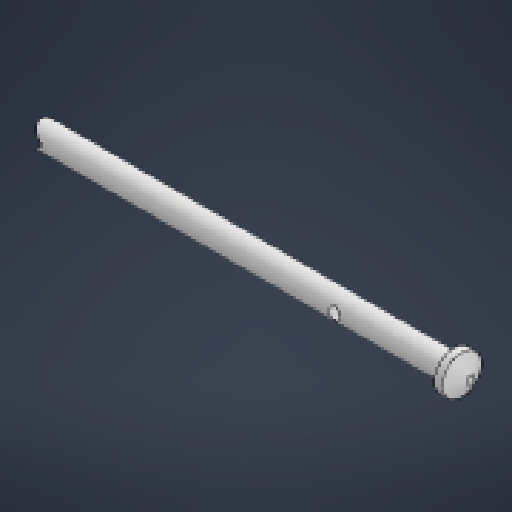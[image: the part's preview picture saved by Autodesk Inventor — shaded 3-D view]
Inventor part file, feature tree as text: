
AUTODESK INVENTOR PART (.ipt)
format: ipt  version: 2025.3 (Build 293356000, 356)  size: 144,384 bytes
history: native  units: mm
features: sketch x1, revolve x1, extrude x1
ambient origin geometry x8: Origin, YZ Plane, XZ Plane, XY Plane, X Axis, Y Axis, Z Axis, Center Point
bodies: Solid1 (feature_tree)
feature tree (3):
  sketch  "Sketch1"  dims[d0=6.0mm d1=3.0mm d2=60.0deg d3=2.0mm d4=10.0mm d5=2.0mm d6=110.0mm d7=360.0deg d8=0.0mm d9=0.0mm d10=3.0mm d14=2.5mm d16=31.98mm d13=0.872665mm]
  revolve  "Revolution1"  [1 undecoded]
  extrude  "Extrusion1"  TaperAngle=60.0deg  [1 undecoded]
note: 2 required parameter values undecoded (feature->parameter linkage not recoverable at this tier; creation-order binding heuristic only, values carry confidence <= 0.55)